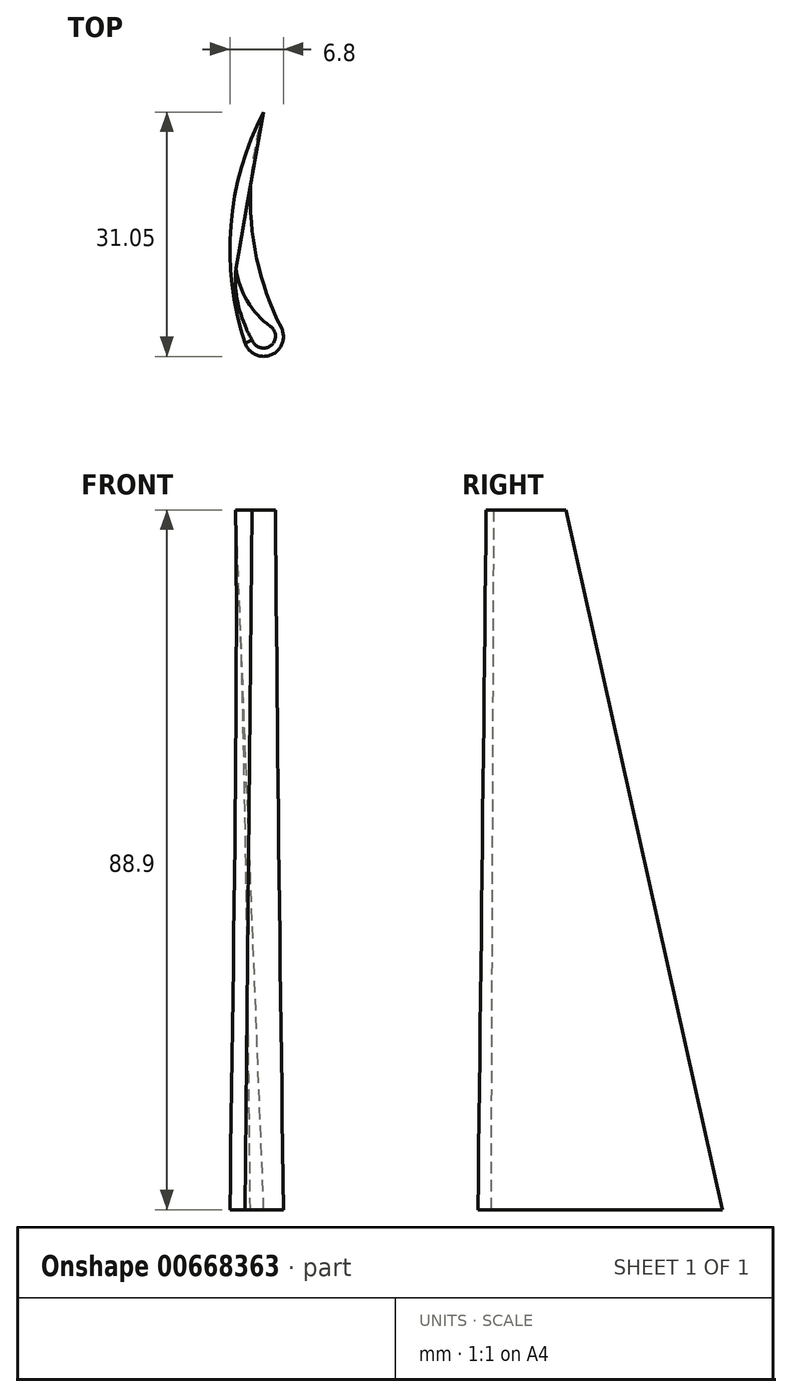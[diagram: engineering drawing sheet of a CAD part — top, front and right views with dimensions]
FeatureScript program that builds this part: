
annotation { "Feature Type Name" : "Feature", "Feature Type Description" : "" }
export const myFeature = defineFeature(function(context is Context, id is Id, definition is map)
    precondition{}
    {
        {
            var Q0;
            Q0=qCreatedBy(makeId("Top.planeOp"),FACE);
            var sketch = newSketch(context, id + "F0", { "sketchPlane" : qUnion([Q0])});
            skCircle(sketch, "E0", {"center": v(0, 0) * mm, "radius": 2.5 * mm});
            skArc(sketch, "E1", {"start": v(0, 28.55) * mm, "mid": v(-4.18, 14.12) * mm, "end": v(-2.37, -0.8) * mm});
            skArc(sketch, "E2", {"start": v(0, 28.55) * mm, "mid": v(-1.58, 14.62) * mm, "end": v(2.23, 1.13) * mm});
            skSolve(sketch);
        }
        {
            var Q0;
            Q0=qCreatedBy(makeId("Top.planeOp"),FACE);
            cPlane(context, id + "F1", {"entities" : qUnion([Q0]), "cplaneType" : CPlaneType.OFFSET, "offset" : 88.9 * mm, "width" : 152.4 * mm, "height" : 152.4 * mm});
        }
        {
            var Q0;
            Q0=qCreatedBy(makeId("Top.planeOp"),FACE);
            var sketch = newSketch(context, id + "F2", { "sketchPlane" : qUnion([Q0])});
            skCircle(sketch, "E3", {"center": v(0, 0) * mm, "radius": 1.52 * mm});
            skSolve(sketch);
        }
        {
            var Q0;
            Q0=qCreatedBy(id+"F1.planeOp",FACE);
            var sketch = newSketch(context, id + "F3", { "sketchPlane" : qUnion([Q0])});
            skCircle(sketch, "E4", {"center": v(-0.03, 0.07) * mm, "radius": 1.52 * mm});
            skArc(sketch, "E5", {"start": v(-3.54, 8.71) * mm, "mid": v(-3.21, 3.97) * mm, "end": v(-1.46, -0.46) * mm});
            skArc(sketch, "E6", {"start": v(-3.54, 8.71) * mm, "mid": v(-2.1, 4.56) * mm, "end": v(0.87, 1.3) * mm});
            skSolve(sketch);
        }
        {
            var Q0;
            Q0 = qSketchRegion(id + "F0", true);
            var Q1;
            Q1 = qSketchRegion(id + "F3", true);
            loft(context, id + "F4", {"sheetProfilesArray" : [{ "sheetProfileEntities" : qUnion([Q0]) }, { "sheetProfileEntities" : qUnion([Q1]) }]});
        }
        {
            var Q0;
            Q0 = qSketchRegion(id + "F2", true);
            extrude(context, id + "F5", {"entities" : qUnion([Q0]), "operationType" : NewBodyOperationType.ADD, "depth" : 25.4 * mm, "offsetDistance" : 25.4 * mm});
        }
    });
